# Revit family: Контейнерная площадка для ТБО «МАФ - 7» Арт 13901
name_source: partatom
category: Антураж
revit_build: Autodesk Revit 2018 (Build: 20180423_1000(x64)
units: mm (PartAtom-declared; Revit-internal decimal feet)

## family parameters
Всегда вертикально = Да
Источник визуального образа = Геометрия семейства
На основе рабочей плоскости = Нет
Общий = Нет
При загрузке вырезать с полостями = Нет
Точка расчета площади = Нет

## types (2) — shared parameters
URL = https://hobbyka.ru
Артикул товара = Арт. 13901
Высота = 2660 мм
Группа модели = Контейнерные площадки для ТБО
Изготовитель = ООО «Хоббика»
Изображение типоразмера = Контейнерная площадка для ТБО «МАФ - 7» Арт 13901.jpeg
Материал изделия = Сталь
Материал крыши = Материал крыши
Цвет каркаса = Сталь
Ширина = 2300 мм

## per-type parameters (varying)
| type | 2 контейнера | 4 контейнера | Длина | Описание |
| Модель на 2 контейнера | Да | Нет | 3220 мм | Контейнерная площадка для ТБО «МАФ - 7». Модель на 2 контейнера |
| Модель на 4 контейнера | Нет | Да | 7500 мм | Контейнерная площадка для ТБО «МАФ - 7». Модель на 4 контейнера |
